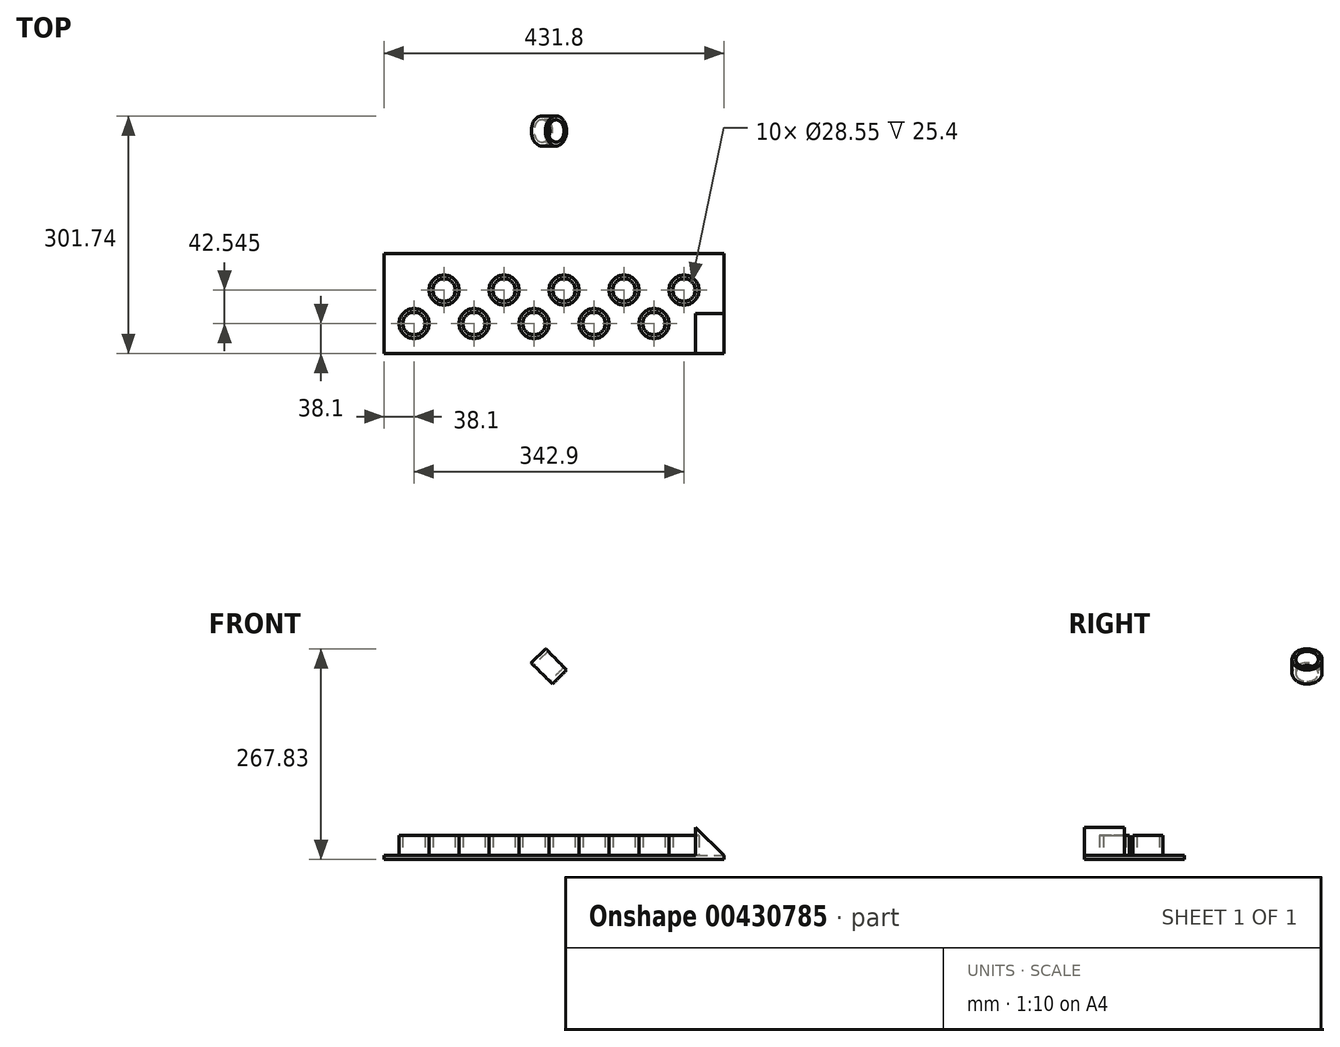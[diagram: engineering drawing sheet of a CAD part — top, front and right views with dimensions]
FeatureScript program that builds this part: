
annotation { "Feature Type Name" : "Feature", "Feature Type Description" : "" }
export const myFeature = defineFeature(function(context is Context, id is Id, definition is map)
    precondition{}
    {
        {
            var Q0;
            Q0=qCreatedBy(makeId("Top.planeOp"),FACE);
            var sketch = newSketch(context, id + "F0", { "sketchPlane" : qUnion([Q0])});
            skLineSegment(sketch, "E0.bottom", {"start": v(0, 0) * mm, "end": v(431.8, 0) * mm});
            skLineSegment(sketch, "E0.top", {"start": v(0, 127) * mm, "end": v(431.8, 127) * mm});
            skLineSegment(sketch, "E0.left", {"start": v(0, 0) * mm, "end": v(0, 127) * mm});
            skLineSegment(sketch, "E0.right", {"start": v(431.8, 0) * mm, "end": v(431.8, 127) * mm});
            skSolve(sketch);
        }
        {
            var Q0;
            Q0=makeQuery(id+"F0.imprint","IMPRINT",FACE,{"disambiguationData":[TD([[makeQuery(id+"F0.imprint","IMPRINT",EDGE,{"derivedFrom":sQuery(id+"F0.wireOp",EDGE,"E0.bottom")}),1.0]])]});
            extrude(context, id + "F1", {"entities" : qUnion([Q0]), "depth" : 5.08 * mm});
        }
        {
            var Q0;
            Q0=makeQuery(id+"F1.opExtrude","CAP_FACE",FACE,{"disambiguationData":[OSD([sQuery(id+"F0.wireOp",EDGE,"E0.bottom"),sQuery(id+"F0.wireOp",EDGE,"E0.top"),sQuery(id+"F0.wireOp",EDGE,"E0.left"),sQuery(id+"F0.wireOp",EDGE,"E0.right")])],"isStart":false});
            var sketch = newSketch(context, id + "F2", { "sketchPlane" : qUnion([Q0])});
            skCircle(sketch, "E1", {"center": v(38.1, 38.1) * mm, "radius": 14.27 * mm});
            skCircle(sketch, "E2", {"center": v(38.1, 38.1) * mm, "radius": 19.05 * mm});
            skCircle(sketch, "E3.0.1.0", {"center": v(76.2, 80.65) * mm, "radius": 14.27 * mm});
            skCircle(sketch, "E3.0.1.1", {"center": v(76.2, 80.65) * mm, "radius": 19.05 * mm});
            skCircle(sketch, "E3.1.0.0", {"center": v(114.3, 38.1) * mm, "radius": 14.27 * mm});
            skCircle(sketch, "E3.1.0.1", {"center": v(114.3, 38.1) * mm, "radius": 19.05 * mm});
            skCircle(sketch, "E3.1.1.0", {"center": v(152.4, 80.65) * mm, "radius": 14.27 * mm});
            skCircle(sketch, "E3.1.1.1", {"center": v(152.4, 80.65) * mm, "radius": 19.05 * mm});
            skCircle(sketch, "E3.2.0.0", {"center": v(190.5, 38.1) * mm, "radius": 14.27 * mm});
            skCircle(sketch, "E3.2.0.1", {"center": v(190.5, 38.1) * mm, "radius": 19.05 * mm});
            skCircle(sketch, "E3.2.1.0", {"center": v(228.6, 80.65) * mm, "radius": 14.27 * mm});
            skCircle(sketch, "E3.2.1.1", {"center": v(228.6, 80.65) * mm, "radius": 19.05 * mm});
            skCircle(sketch, "E3.3.0.0", {"center": v(266.7, 38.1) * mm, "radius": 14.27 * mm});
            skCircle(sketch, "E3.3.0.1", {"center": v(266.7, 38.1) * mm, "radius": 19.05 * mm});
            skCircle(sketch, "E3.3.1.0", {"center": v(304.8, 80.65) * mm, "radius": 14.27 * mm});
            skCircle(sketch, "E3.3.1.1", {"center": v(304.8, 80.65) * mm, "radius": 19.05 * mm});
            skCircle(sketch, "E3.4.0.0", {"center": v(342.9, 38.1) * mm, "radius": 14.27 * mm});
            skCircle(sketch, "E3.4.0.1", {"center": v(342.9, 38.1) * mm, "radius": 19.05 * mm});
            skCircle(sketch, "E3.4.1.0", {"center": v(381, 80.65) * mm, "radius": 14.27 * mm});
            skCircle(sketch, "E3.4.1.1", {"center": v(381, 80.65) * mm, "radius": 19.05 * mm});
            skLineSegment(sketch, "E3.direction1", {"start": v(38.1, 38.1) * mm, "end": v(114.3, 38.1) * mm, "construction": true});
            skLineSegment(sketch, "E3.direction2", {"start": v(38.1, 38.1) * mm, "end": v(76.2, 80.65) * mm, "construction": true});
            skLineSegment(sketch, "E4", {"start": v(76.2, 38.1) * mm, "end": v(76.2, 80.65) * mm, "construction": true});
            skSolve(sketch);
        }
        {
            var Q0;
            Q0=qSketchRegion(id+"F2",true);
            extrude(context, id + "F3", {"entities" : qUnion([Q0]), "operationType" : NewBodyOperationType.ADD, "depth" : 25.4 * mm});
        }
        {
            var Q0;
            Q0=makeQuery(id+"F1.opExtrude","SWEPT_FACE",FACE,{"disambiguationData":[OSD([sQuery(id+"F0.wireOp",EDGE,"E0.bottom")])]});
            var sketch = newSketch(context, id + "F4", { "sketchPlane" : qUnion([Q0])});
            skLineSegment(sketch, "E5", {"start": v(395.88, 41) * mm, "end": v(431.8, 5.08) * mm});
            skLineSegment(sketch, "E6", {"start": v(431.8, 5.08) * mm, "end": v(395.88, 5.08) * mm});
            skLineSegment(sketch, "E7", {"start": v(395.88, 5.08) * mm, "end": v(395.88, 41) * mm});
            skSolve(sketch);
        }
        {
            var Q0;
            Q0=makeQuery(id+"F4.imprint","IMPRINT",FACE,{"disambiguationData":[TD([[makeQuery(id+"F4.imprint","IMPRINT",EDGE,{"derivedFrom":sQuery(id+"F4.wireOp",EDGE,"E5")}),-1.0]])]});
            var Q1;
            {var subQ0=sQuery(id+"F4.wireOp",EDGE,"CnTXyRIH-NC53-LO1l-I5cS-RCVd2I7XrNuE");var subQ1=sQuery(id+"F4.wireOp",EDGE,"E5");var subQ2=makeQuery(id+"F4.imprint","INTERSECT",VERTEX,{"derivedFrom":[subQ1,subQ0]});Q1=makeQuery(id+"F4.imprint","IMPRINT",FACE,{"disambiguationData":[TD([[makeQuery(id+"F4.imprint","IMPRINT",EDGE,{"disambiguationData":[TD([[subQ2,1.0]])],"derivedFrom":subQ1}),1.0]])]});}
            var Q2;
            {var subQ0=sQuery(id+"F4.wireOp",EDGE,"E6");Q2=makeQuery(id+"F4.imprint","IMPRINT",FACE,{"disambiguationData":[TD([[makeQuery(id+"F4.imprint","IMPRINT",EDGE,{"derivedFrom":subQ0}),-1.0]])]});}
            extrude(context, id + "F5", {"entities" : qUnion([Q0, Q1, Q2]), "operationType" : NewBodyOperationType.ADD, "oppositeDirection" : true, "depth" : 50.8 * mm});
        }
        {
            var Q0;
            {var subQ0=sQuery(id+"F4.wireOp",EDGE,"E5");Q0=makeQuery(id+"F5.opExtrude","SWEPT_FACE",FACE,{"disambiguationData":[OSD([subQ0]),TDD([makeQuery(id+"F4.imprint","IMPRINT",EDGE,{"disambiguationData":[TD([[makeQuery(id+"F4.imprint","INTERSECT",VERTEX,{"derivedFrom":[subQ0,sQuery(id+"F4.wireOp",EDGE,"CnTXyRIH-NC53-LO1l-I5cS-RCVd2I7XrNuE")]}),1.0]])],"derivedFrom":subQ0})])]});}
            var sketch = newSketch(context, id + "F6", { "sketchPlane" : qUnion([Q0])});
            skCircle(sketch, "E8.2.0.0", {"center": v(282.69, 25.4) * mm, "radius": 14.29 * mm});
            skCircle(sketch, "E8.2.0.1", {"center": v(282.69, 25.4) * mm, "radius": 19.05 * mm});
            skPoint(sketch, "E9", {"position": v(301.74, 25.4) * mm});
            skSolve(sketch);
        }
        {
            var Q0;
            Q0=makeQuery(id+"F6.imprint","IMPRINT",FACE,{"disambiguationData":[TD([[makeQuery(id+"F6.imprint","IMPRINT",EDGE,{"derivedFrom":sQuery(id+"F6.wireOp",EDGE,"E8.2.0.0")}),-1.0]])]});
            extrude(context, id + "F7", {"entities" : qUnion([Q0]), "operationType" : NewBodyOperationType.ADD, "depth" : 25.4 * mm});
        }
    });
